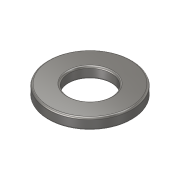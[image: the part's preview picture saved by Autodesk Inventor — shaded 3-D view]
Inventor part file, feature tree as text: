
AUTODESK INVENTOR PART (.ipt)
format: ipt  version: 2018.2 (Build 222227000, 227)  size: 116,224 bytes
history: native  units: mm
features: extrude x1, fillet x1, sketch x1
ambient origin geometry x8: Origin, YZ Plane, XZ Plane, XY Plane, X Axis, Y Axis, Z Axis, Center Point
bodies: Volumenkörper1 (feature_tree)
feature tree (3):
  extrude  "Extrusion1"  Depth=0.25mm
  fillet  "Rundung1"  Radius=1.6mm
  sketch  "Skizze1"  dims[d0=6.0mm d1=12.0mm d2=1.6mm d3=0.0mm d4=0.25mm]
